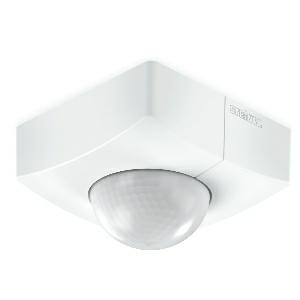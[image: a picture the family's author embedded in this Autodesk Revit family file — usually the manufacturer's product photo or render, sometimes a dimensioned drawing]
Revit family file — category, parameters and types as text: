
# Revit family: is_345_058258
name_source: partatom
category: Elektroinstallationen
revit_build: Autodesk Revit 2016 (Build: 20190508_0715(x64)
units: mm (PartAtom-declared; Revit-internal decimal feet)

## family parameters
Basisbauteil = Fläche
Beim Laden mit Abzugskörper schneiden = Nein
Bemaßung runder Anschluss = Durchmesser verwenden
Beschriftungsausrichtung beibehalten = Nein
Gemeinsam genutzt = Nein
Raumberechnungspunkt = Nein
Teiletyp = Normal

## types (1)
- IS 345
    Apparent Load = 0 VA
    Beschreibung = Type: Motion detectors; Dimensions (L x W x H): 65 x 95 x 95 mm; Power supply, detail: KNX bus; Sensor Technology: passive infrared; Application, place: Outdoors, Indoors; Application, room: corridor / aisle, multi-storey / underground car park, outdoors, Indoors; Installation site: ceiling; Installation: Surface wiring; Electronic scalability: No; Mechanical scalability: No; Mounting height: 2,50 – 5,00 m; Optimum mounting height: 2,8 m; Detection angle: 360 °; Angle of aperture: 45 °; Sneak-by guard: Yes; Capability of masking out individual segments: Yes; Reach, radial: 12 x 6 m (72 m²); Reach, tangential: 23 x 6 m (138 m²); Twilight setting TEACH: Yes; Twilight setting: 2 – 1000 lx; Time setting: 0 sec – 1092 min; Basic light level function: Yes; KNX functions: Photo-cell controller, Basic light level function, Light level, HVAC output, Constant-lighting control, Light output 2x, Presence output, Day / night function; With bus coupling: Yes; Settings via: ETS software, Remote control, Bus, Smart Remote; IP-rating: IP54; Material: Plastic; Colour: white; Colour, RAL: 9003; Manufacturer's Warranty: 5 years; Version: KNX - surface, sq.; PU1, EAN: 4007841058258
    Height = 95 mm
    Hersteller = Steinel
    Length = 65 mm
    Maximum range = 11.589 m
    ModVariant = Nein
    Modell = 058258
    Mounting Place = Ceiling
    Mounting Type = Surface mounted
    Number of Poles = 1
    OnlyDefault = Ja
    Power Factor = 1
    Product Name = IS 345
    Product group = Sensor-switched outdoor light
    ProductGroupID = 3
    Protection Class = Protection class II
    Protection Degree = IP 54
    RlxData = <blob elided: 163913 chars, md5=66882e93>
    Sensor characteristics = Stretched
    Sensor type = Passive (infrared)
    SensorDataFile = <blob elided: 5885 chars, md5=98bccc25>
    Type of entry = Motion
    Typenbild = produkt1_058258.jpg
    Typenkommentare = Product without accessories
    URL = http://relux.com
    VarID = ---
    Voltage = 0 V
    Vorgabe-Ansicht = 1800 mm
    Weight = 0.00 kg
    Width = 95 mm

## geometry (parser evidence)
native form markers: Blend x4, Sweep x16
no freeform markers — native parametric forms only
